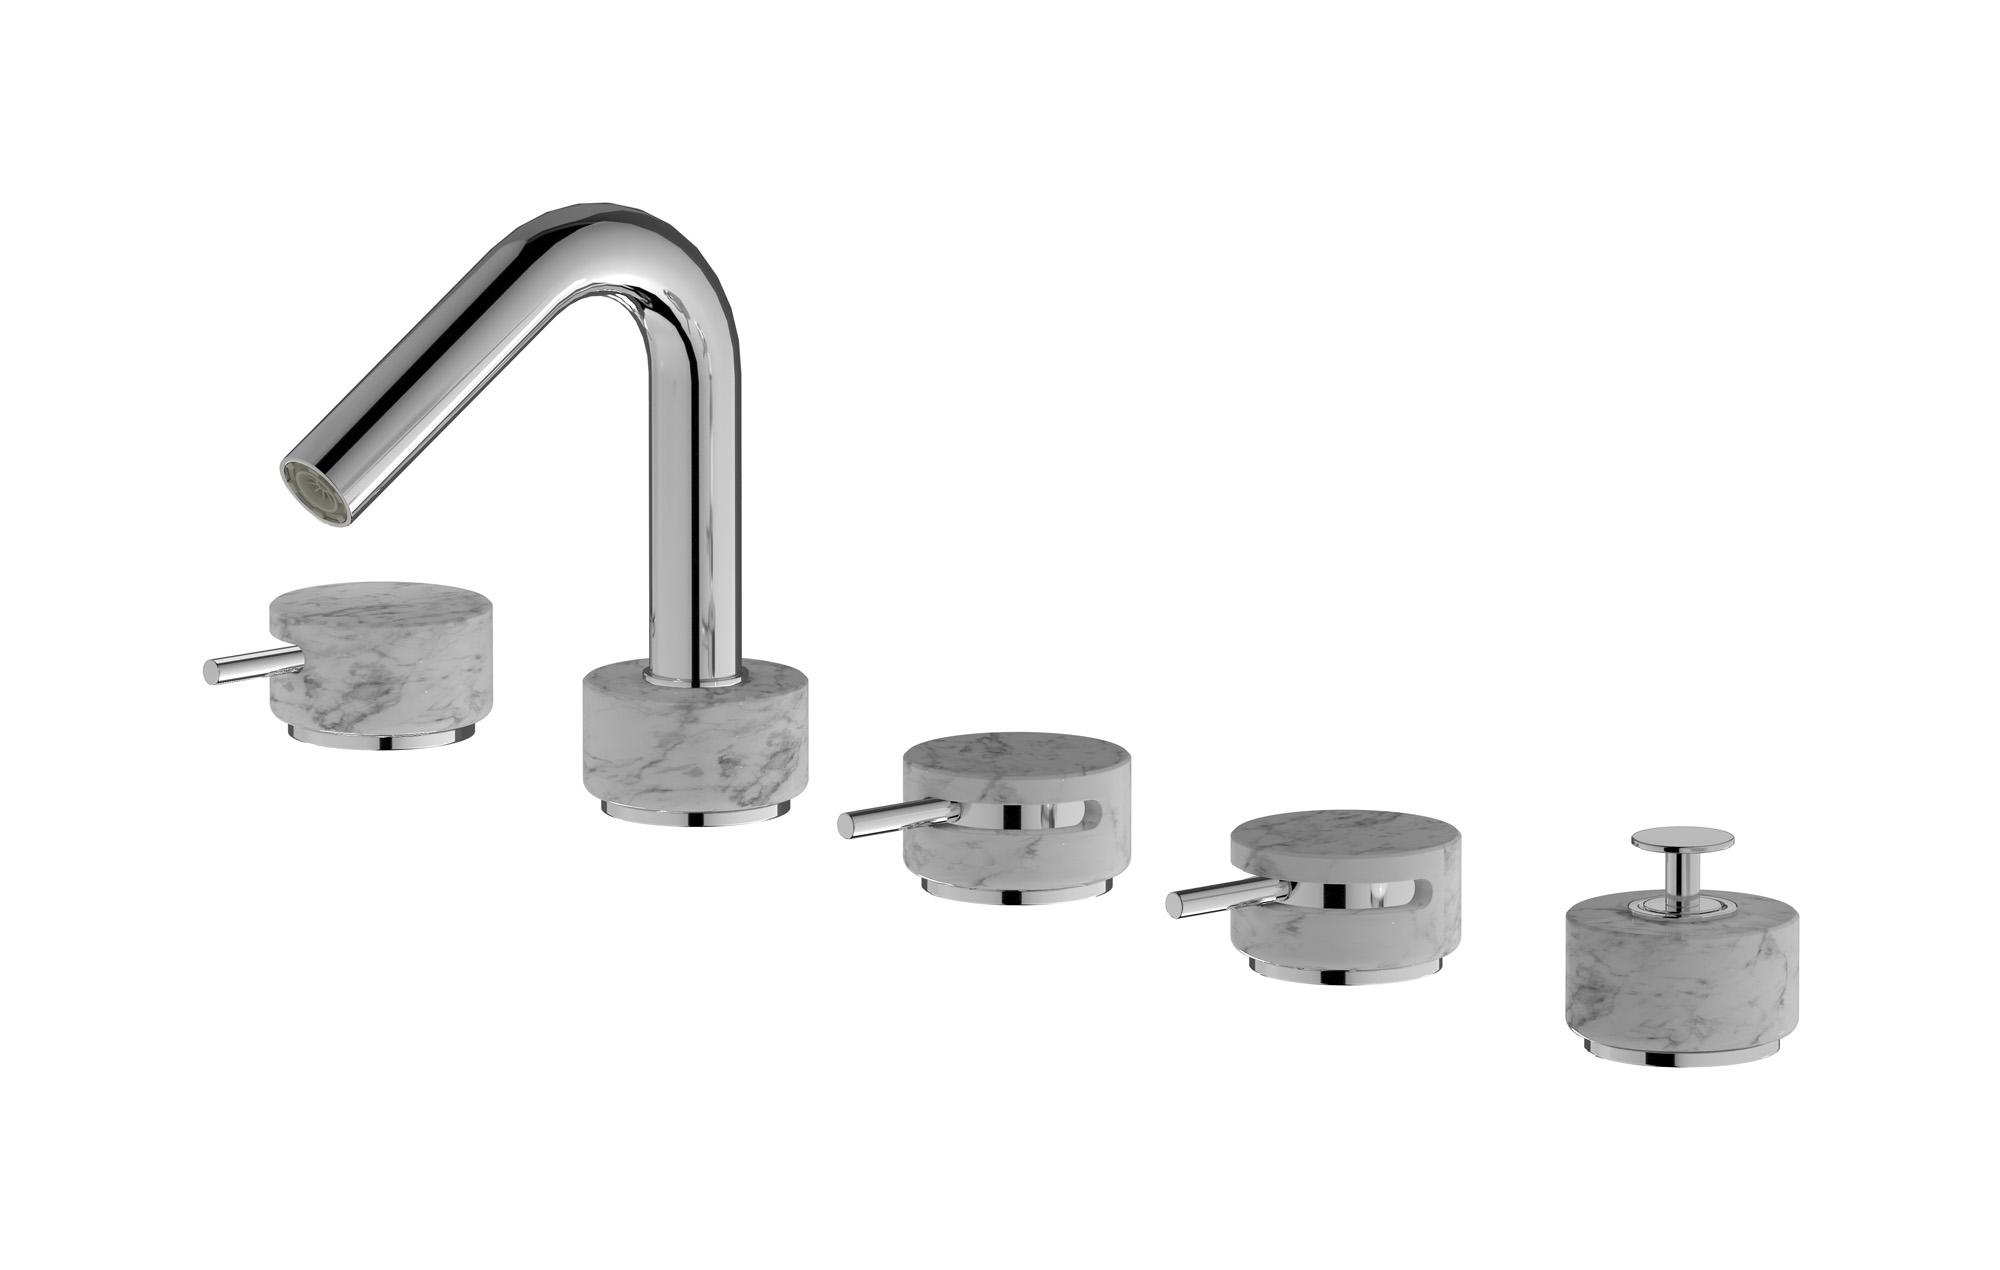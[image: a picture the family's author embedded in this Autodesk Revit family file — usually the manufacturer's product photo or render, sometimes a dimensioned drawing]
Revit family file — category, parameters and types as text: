
# Revit family: MR396_1
name_source: partatom
category: Apparecchi idraulici
units: mm (PartAtom-declared; Revit-internal decimal feet)

## family parameters
Basato su piano di lavoro = No
Condiviso = No
Mantieni orientamento annotazione = No
Numero OmniClass = 23.45.55.17
Punto di calcolo locali = No
Quota connettore circolare = Usa diametro
Sempre verticale = Sì
Taglio con vuoti quando caricato = No
Tipo di parte = Normale
Titolo OmniClass = Mixing Faucets

## types (14) — shared parameters
Cold water inlet = 10 mm  [stored 0.0328084 ft]
Commenti sul tipo = Bath filler
Connessione CW = No
Connessione HW = No
Connessione di scarico = No
Connessione di ventilazione = No
Descrizione = Five holes deck mounted bath filler with shower kit
Hot water inlet = 10 mm  [stored 0.0328084 ft]
Produttore = IB Rubinetterie S.p.A.
URL = https://www.weareib.it
zero-valued in all types: Prospetto di default

## per-type parameters (varying)
| type | Finishes surface | Immagine tipo | Modello |
| Chrome | IB_Chrome | MR396CC_1.jpg | MR396CC_1 |
| Platinum | IB_Platinum | MR396PL_1.jpg | MR396PL_1 |
| Brushed nickel | IB_Brushed nickel | MR396SS_1.jpg | MR396SS_1 |
| Natural brass | IB_Brass | MR396ON_1.jpg | MR396ON_1 |
| Matt white | IB_matt white | MR396BO_1.jpg | MR396BO_1 |
| Matt black | IB_matt black | MR396NP_1.jpg | MR396NP_1 |
| Black chrome | IB_Black chrome | MR396CF_1.jpg | MR396CF_1 |
| Brushed black chrome | IB_Brushed black chrome | MR396CS_1.jpg | MR396CS_1 |
| Pale gold | IB_Pale gold | MR396II_1.jpg | MR396II_1 |
| Brushed pale gold | IB_brushed pale gold | MR396IS_1.jpg | MR396IS_1 |
| Rose gold | IB_Rose gold | MR396RS_1.jpg | MR396RS_1 |
| Brushed rose gold | IB_Brushed rose gold | MR396SR_1.jpg | MR396SR_1 |
| Gold | IB_gold | MR396OO_1.jpg | MR396OO_1 |
| Brushed gold | IB_brushed gold | MR396OS_1.jpg | MR396OS_1 |

note: [stored X ft] marks values corroborated as IEEE doubles in the binary element streams (Revit-internal decimal feet)
